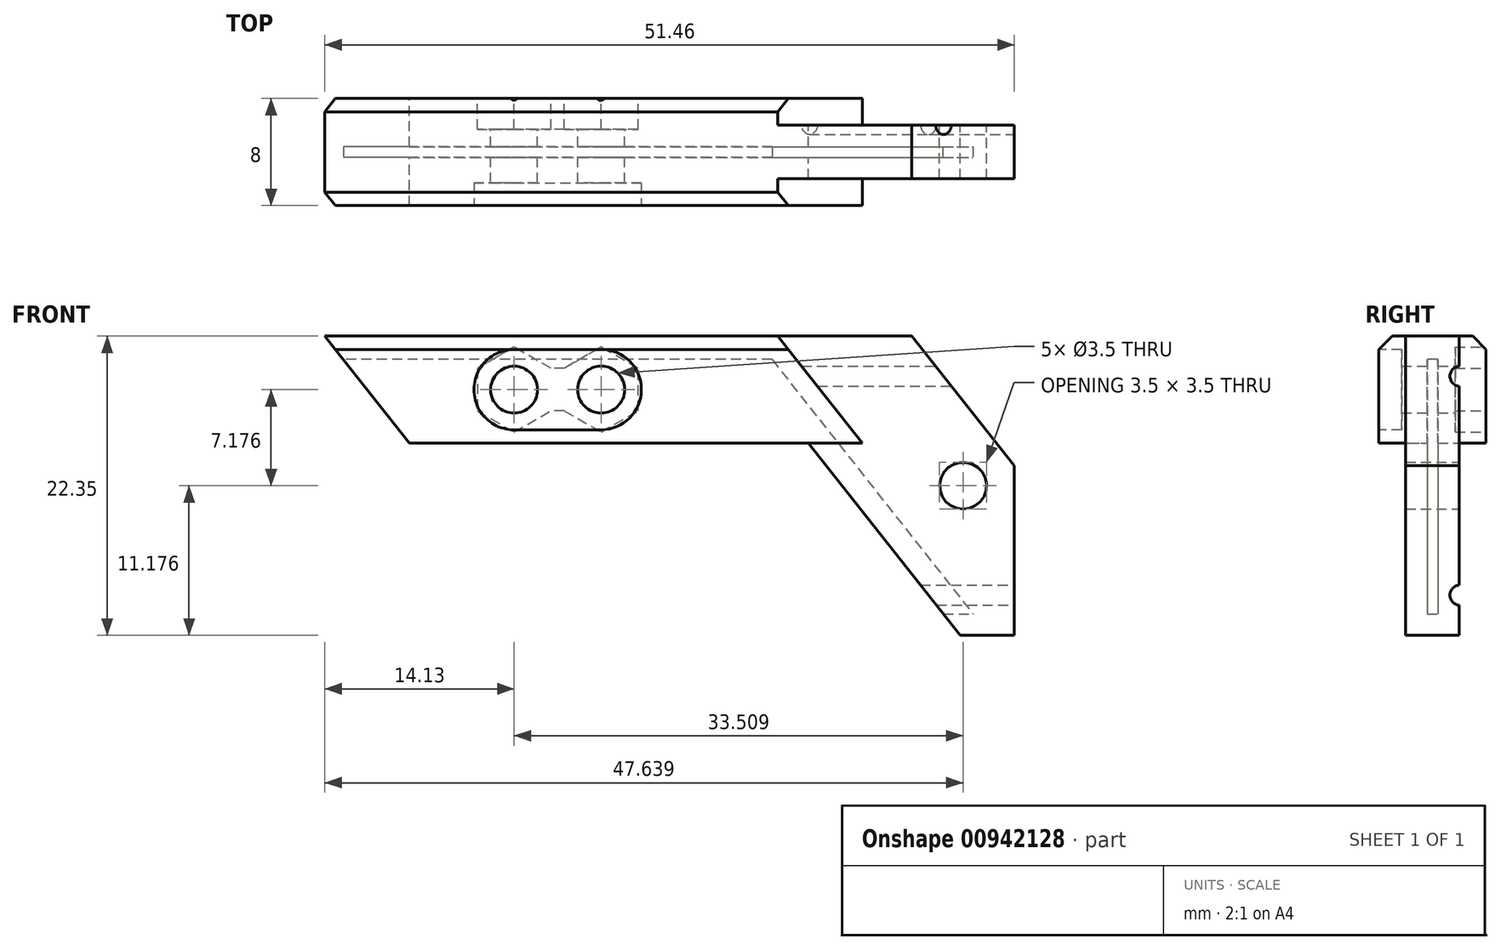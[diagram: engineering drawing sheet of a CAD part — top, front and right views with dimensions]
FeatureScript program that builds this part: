
annotation { "Feature Type Name" : "Feature", "Feature Type Description" : "" }
export const myFeature = defineFeature(function(context is Context, id is Id, definition is map)
    precondition{}
    {
        {
            var Q0;
            Q0=qCreatedBy(makeId("Front.planeOp"),FACE);
            var sketch = newSketch(context, id + "F0", { "sketchPlane" : qUnion([Q0])});
            skLineSegment(sketch, "E0", {"start": v(-31, 0) * mm, "end": v(31, 0) * mm});
            skLineSegment(sketch, "E1", {"start": v(31, 0) * mm, "end": v(31, 19) * mm, "construction": true});
            skLineSegment(sketch, "E2", {"start": v(31, 19) * mm, "end": v(-31, 19) * mm});
            skLineSegment(sketch, "E3", {"start": v(-16, 19) * mm, "end": v(16, 19) * mm});
            skPoint(sketch, "E4", {"position": v(0, 19) * mm});
            skLineSegment(sketch, "E5", {"start": v(16, 19) * mm, "end": v(31, 0) * mm});
            skLineSegment(sketch, "E6", {"start": v(-16, 19) * mm, "end": v(-31, 0) * mm});
            skLineSegment(sketch, "E7", {"start": v(-3.25, 19) * mm, "end": v(3.25, 19) * mm, "construction": true});
            skLineSegment(sketch, "E8", {"start": v(-3.25, 19) * mm, "end": v(-3.25, 15) * mm, "construction": true});
            skLineSegment(sketch, "E9", {"start": v(3.25, 19) * mm, "end": v(3.25, 15) * mm, "construction": true});
            skCircle(sketch, "E10", {"center": v(-3.25, 16.75) * mm, "radius": 1.75 * mm});
            skCircle(sketch, "E11", {"center": v(3.25, 16.75) * mm, "radius": 1.75 * mm});
            skLineSegment(sketch, "E12", {"start": v(-5, 16.81) * mm, "end": v(-5, 19) * mm});
            skLineSegment(sketch, "E13", {"start": v(-1.5, 16.8) * mm, "end": v(-1.5, 19) * mm});
            skLineSegment(sketch, "E14", {"start": v(1.5, 16.8) * mm, "end": v(1.5, 19) * mm});
            skLineSegment(sketch, "E15", {"start": v(5, 16.85) * mm, "end": v(5, 19) * mm});
            skSolve(sketch);
        }
        {
            var Q0;
            Q0=qCreatedBy(makeId("Front.planeOp"),FACE);
            var sketch = newSketch(context, id + "F1", { "sketchPlane" : qUnion([Q0])});
            skLineSegment(sketch, "E16.0.0", {"start": v(5, 19) * mm, "end": v(5, 16.85) * mm, "construction": true});
            skArc(sketch, "E16.0.1", {"start": v(5, 16.85) * mm, "mid": v(3.28, 15) * mm, "end": v(1.5, 16.8) * mm, "construction": true});
            skLineSegment(sketch, "E16.0.2", {"start": v(1.5, 16.8) * mm, "end": v(1.5, 19) * mm, "construction": true});
            skLineSegment(sketch, "E16.0.3", {"start": v(1.5, 19) * mm, "end": v(-1.5, 19) * mm, "construction": true});
            skLineSegment(sketch, "E16.0.4", {"start": v(-1.5, 19) * mm, "end": v(-1.5, 16.8) * mm, "construction": true});
            skArc(sketch, "E16.0.5", {"start": v(-1.5, 16.8) * mm, "mid": v(-3.26, 15) * mm, "end": v(-5, 16.81) * mm, "construction": true});
            skLineSegment(sketch, "E16.0.6", {"start": v(-5, 16.81) * mm, "end": v(-5, 19) * mm, "construction": true});
            skLineSegment(sketch, "E16.0.7", {"start": v(-5, 19) * mm, "end": v(-16, 19) * mm, "construction": true});
            skLineSegment(sketch, "E16.0.8", {"start": v(-16, 19) * mm, "end": v(-31, 0) * mm, "construction": true});
            skLineSegment(sketch, "E16.0.9", {"start": v(-31, 0) * mm, "end": v(31, 0) * mm, "construction": true});
            skLineSegment(sketch, "E16.0.10", {"start": v(31, 0) * mm, "end": v(16, 19) * mm, "construction": true});
            skLineSegment(sketch, "E16.0.11", {"start": v(16, 19) * mm, "end": v(5, 19) * mm, "construction": true});
            skLineSegment(sketch, "E17", {"start": v(-31, 0) * mm, "end": v(31, 0) * mm});
            skLineSegment(sketch, "E18", {"start": v(16, 19) * mm, "end": v(-16, 19) * mm});
            skLineSegment(sketch, "E19", {"start": v(-16, 19) * mm, "end": v(-31, 0) * mm});
            skLineSegment(sketch, "E20", {"start": v(16, 19) * mm, "end": v(31, 0) * mm});
            skSolve(sketch);
        }
        {
            var Q0;
            Q0=qCreatedBy(makeId("Front.planeOp"),FACE);
            var sketch = newSketch(context, id + "F2", { "sketchPlane" : qUnion([Q0])});
            skLineSegment(sketch, "E21.0.0", {"start": v(5, 19) * mm, "end": v(5, 16.85) * mm, "construction": true});
            skArc(sketch, "E21.0.1", {"start": v(5, 16.85) * mm, "mid": v(3.28, 15) * mm, "end": v(1.5, 16.8) * mm, "construction": true});
            skLineSegment(sketch, "E21.0.2", {"start": v(1.5, 16.8) * mm, "end": v(1.5, 19) * mm, "construction": true});
            skLineSegment(sketch, "E21.0.3", {"start": v(1.5, 19) * mm, "end": v(-1.5, 19) * mm, "construction": true});
            skLineSegment(sketch, "E21.0.4", {"start": v(-1.5, 19) * mm, "end": v(-1.5, 16.8) * mm, "construction": true});
            skArc(sketch, "E21.0.5", {"start": v(-1.5, 16.8) * mm, "mid": v(-3.26, 15) * mm, "end": v(-5, 16.81) * mm, "construction": true});
            skLineSegment(sketch, "E21.0.6", {"start": v(-5, 16.81) * mm, "end": v(-5, 19) * mm, "construction": true});
            skLineSegment(sketch, "E21.0.7", {"start": v(-5, 19) * mm, "end": v(-16, 19) * mm, "construction": true});
            skLineSegment(sketch, "E21.0.8", {"start": v(-16, 19) * mm, "end": v(-31, 0) * mm, "construction": true});
            skLineSegment(sketch, "E21.0.9", {"start": v(-31, 0) * mm, "end": v(31, 0) * mm, "construction": true});
            skLineSegment(sketch, "E21.0.10", {"start": v(31, 0) * mm, "end": v(16, 19) * mm, "construction": true});
            skLineSegment(sketch, "E21.0.11", {"start": v(16, 19) * mm, "end": v(5, 19) * mm, "construction": true});
            skLineSegment(sketch, "E22.0", {"start": v(-3.25, 19) * mm, "end": v(-3.25, 15) * mm, "construction": true});
            skLineSegment(sketch, "E22.1", {"start": v(31, 0) * mm, "end": v(31, 19) * mm, "construction": true});
            skLineSegment(sketch, "E22.2", {"start": v(3.25, 19) * mm, "end": v(3.25, 15) * mm, "construction": true});
            skLineSegment(sketch, "E22.3", {"start": v(31, 19) * mm, "end": v(-31, 19) * mm, "construction": true});
            skLineSegment(sketch, "E22.4", {"start": v(-16, 19) * mm, "end": v(16, 19) * mm, "construction": true});
            skCircle(sketch, "E22.5", {"center": v(-3.25, 16.75) * mm, "radius": 1.75 * mm, "construction": true});
            skCircle(sketch, "E22.6", {"center": v(3.25, 16.75) * mm, "radius": 1.75 * mm, "construction": true});
            skLineSegment(sketch, "E22.7", {"start": v(-3.25, 19) * mm, "end": v(3.25, 19) * mm, "construction": true});
            skLineSegment(sketch, "E22.10", {"start": v(-1.5, 16.8) * mm, "end": v(-1.5, 19) * mm, "construction": true});
            skLineSegment(sketch, "E22.11", {"start": v(16, 19) * mm, "end": v(31, 0) * mm, "construction": true});
            skLineSegment(sketch, "E22.14", {"start": v(5, 16.85) * mm, "end": v(5, 19) * mm, "construction": true});
            skCircle(sketch, "E23", {"center": v(-3.25, 16.75) * mm, "radius": 1.75 * mm});
            skCircle(sketch, "E24", {"center": v(3.25, 16.75) * mm, "radius": 1.75 * mm});
            skLineSegment(sketch, "E25", {"start": v(-16, 19) * mm, "end": v(-11.07, 12.75) * mm});
            skLineSegment(sketch, "E26", {"start": v(-11.07, 12.75) * mm, "end": v(20.93, 12.75) * mm});
            skCircle(sketch, "E27", {"center": v(-3.25, 16.75) * mm, "radius": 3 * mm});
            skCircle(sketch, "E28", {"center": v(3.25, 16.75) * mm, "radius": 3 * mm});
            skLineSegment(sketch, "E29", {"start": v(-16, 19) * mm, "end": v(-17.38, 20.75) * mm});
            skLineSegment(sketch, "E30", {"start": v(-17.38, 20.75) * mm, "end": v(14.62, 20.75) * mm});
            skLineSegment(sketch, "E31", {"start": v(16, 19) * mm, "end": v(14.62, 20.75) * mm});
            skLineSegment(sketch, "E32", {"start": v(18.72, 12.75) * mm, "end": v(30.05, -1.6) * mm});
            skLineSegment(sketch, "E33", {"start": v(30.05, -1.6) * mm, "end": v(34.08, -1.6) * mm});
            skLineSegment(sketch, "E34", {"start": v(34.08, -1.6) * mm, "end": v(16.44, 20.75) * mm});
            skLineSegment(sketch, "E35", {"start": v(16.44, 20.75) * mm, "end": v(14.62, 20.75) * mm});
            skLineSegment(sketch, "E36", {"start": v(16.44, 20.75) * mm, "end": v(26.44, 20.75) * mm});
            skLineSegment(sketch, "E37", {"start": v(26.44, 20.75) * mm, "end": v(44.08, -1.6) * mm});
            skLineSegment(sketch, "E38", {"start": v(22.75, 12.75) * mm, "end": v(32.75, 12.75) * mm});
            skLineSegment(sketch, "E39", {"start": v(32.75, 12.75) * mm, "end": v(26.44, 20.75) * mm});
            skLineSegment(sketch, "E40", {"start": v(16.44, 20.75) * mm, "end": v(22.75, 12.75) * mm});
            skLineSegment(sketch, "E41", {"start": v(37.84, -1.6) * mm, "end": v(37.84, 20.75) * mm, "construction": true});
            skLineSegment(sketch, "E42", {"start": v(37.84, 9.58) * mm, "end": v(14.7, 9.58) * mm, "construction": true});
            skLineSegment(sketch, "E43", {"start": v(25.26, 9.58) * mm, "end": v(35.26, 9.58) * mm, "construction": true});
            skCircle(sketch, "E44", {"center": v(30.26, 9.58) * mm, "radius": 1.75 * mm});
            skLineSegment(sketch, "E45", {"start": v(18.72, 12.75) * mm, "end": v(22.75, 12.75) * mm});
            skLineSegment(sketch, "E46", {"start": v(22.75, 12.75) * mm, "end": v(16.44, 20.75) * mm});
            skLineSegment(sketch, "E47", {"start": v(34.08, -1.6) * mm, "end": v(34.08, 11.07) * mm});
            skSolve(sketch);
        }
        {
            var Q0;
            Q0=qCreatedBy(makeId("Front.planeOp"),FACE);
            var sketch = newSketch(context, id + "F3", { "sketchPlane" : qUnion([Q0])});
            skLineSegment(sketch, "E48.0.0", {"start": v(14.62, 20.75) * mm, "end": v(14.62, 20.75) * mm});
            skLineSegment(sketch, "E48.0.1", {"start": v(14.62, 20.75) * mm, "end": v(-17.38, 20.75) * mm, "construction": true});
            skLineSegment(sketch, "E48.0.2", {"start": v(-17.38, 20.75) * mm, "end": v(-16, 19) * mm, "construction": true});
            skLineSegment(sketch, "E48.0.3", {"start": v(-16, 19) * mm, "end": v(-11.07, 12.75) * mm, "construction": true});
            skLineSegment(sketch, "E48.0.4", {"start": v(-11.07, 12.75) * mm, "end": v(18.72, 12.75) * mm, "construction": true});
            skLineSegment(sketch, "E48.0.5", {"start": v(18.72, 12.75) * mm, "end": v(30.05, -1.6) * mm, "construction": true});
            skLineSegment(sketch, "E48.0.6", {"start": v(30.05, -1.6) * mm, "end": v(34.08, -1.6) * mm, "construction": true});
            skLineSegment(sketch, "E48.0.7", {"start": v(34.08, -1.6) * mm, "end": v(16.44, 20.75) * mm, "construction": true});
            skLineSegment(sketch, "E49", {"start": v(30.05, -1.6) * mm, "end": v(18.72, 12.75) * mm});
            skLineSegment(sketch, "E50", {"start": v(-11.07, 12.75) * mm, "end": v(-17.38, 20.75) * mm});
            skLineSegment(sketch, "E51", {"start": v(-35.67, -1.6) * mm, "end": v(30.05, -1.6) * mm});
            skLineSegment(sketch, "E52", {"start": v(-11.07, 12.75) * mm, "end": v(18.72, 12.75) * mm});
            skLineSegment(sketch, "E53", {"start": v(-17.38, 20.75) * mm, "end": v(-35.67, -1.6) * mm});
            skLineSegment(sketch, "E54", {"start": v(18.72, 12.75) * mm, "end": v(32.74, 12.75) * mm});
            skLineSegment(sketch, "E55", {"start": v(32.74, 12.75) * mm, "end": v(44.07, -1.6) * mm});
            skLineSegment(sketch, "E56", {"start": v(44.07, -1.6) * mm, "end": v(30.05, -1.6) * mm});
            skLineSegment(sketch, "E57", {"start": v(14.62, 20.75) * mm, "end": v(14.62, -1.6) * mm, "construction": true});
            skLineSegment(sketch, "E58", {"start": v(14.62, 9.58) * mm, "end": v(40, 9.58) * mm, "construction": true});
            skLineSegment(sketch, "E59", {"start": v(25.26, 9.58) * mm, "end": v(35.25, 9.58) * mm, "construction": true});
            skCircle(sketch, "E60", {"center": v(30.25, 9.58) * mm, "radius": 1.75 * mm});
            skCircle(sketch, "E61", {"center": v(30.25, 9.58) * mm, "radius": 3 * mm});
            skSolve(sketch);
        }
        {
            var Q0;
            {var subQ3=sQuery(id+"F2.wireOp",EDGE,"E25");Q0=makeQuery(id+"F2.imprint","IMPRINT",FACE,{"disambiguationData":[TD([[makeQuery(id+"F2.imprint","IMPRINT",EDGE,{"derivedFrom":subQ3}),1.0]])]});}
            var Q1;
            Q1=makeQuery(id+"F2.imprint","IMPRINT",FACE,{"disambiguationData":[TD([[makeQuery(id+"F2.imprint","IMPRINT",EDGE,{"derivedFrom":sQuery(id+"F2.wireOp",EDGE,"E24")}),-1.0]])]});
            var Q2;
            Q2=makeQuery(id+"F2.imprint","IMPRINT",FACE,{"disambiguationData":[TD([[makeQuery(id+"F2.imprint","IMPRINT",EDGE,{"derivedFrom":sQuery(id+"F2.wireOp",EDGE,"E23")}),-1.0]])]});
            extrude(context, id + "F4", {"entities" : qUnion([Q0, Q1, Q2]), "depth" : 4 * mm, "offsetDistance" : 25 * mm, "hasSecondDirection" : true, "secondDirectionOppositeDirection" : true, "secondDirectionDepth" : 4 * mm});
        }
        {
            var Q0;
            {var subQ0=sQuery(id+"F2.wireOp",EDGE,"E36");Q0=makeQuery(id+"F2.imprint","IMPRINT",FACE,{"disambiguationData":[TD([[makeQuery(id+"F2.imprint","IMPRINT",EDGE,{"derivedFrom":subQ0}),-1.0]])]});}
            var Q1;
            {var subQ0=sQuery(id+"F2.wireOp",EDGE,"E38");Q1=makeQuery(id+"F2.imprint","IMPRINT",FACE,{"disambiguationData":[TD([[makeQuery(id+"F2.imprint","IMPRINT",EDGE,{"derivedFrom":subQ0}),-1.0]])]});}
            var Q2;
            Q2=makeQuery(id+"F3.imprint","IMPRINT",FACE,{"disambiguationData":[TD([[makeQuery(id+"F3.imprint","IMPRINT",EDGE,{"derivedFrom":sQuery(id+"F3.wireOp",EDGE,"E60")}),-1.0]])]});
            var Q3;
            {var subQ3=sQuery(id+"F2.wireOp",EDGE,"E32");Q3=makeQuery(id+"F2.imprint","IMPRINT",FACE,{"disambiguationData":[TD([[makeQuery(id+"F2.imprint","IMPRINT",EDGE,{"derivedFrom":subQ3}),1.0]])]});}
            extrude(context, id + "F5", {"entities" : qUnion([Q0, Q1, Q2, Q3]), "operationType" : NewBodyOperationType.ADD, "depth" : 2 * mm, "offsetDistance" : 25 * mm, "hasSecondDirection" : true, "secondDirectionOppositeDirection" : true, "secondDirectionDepth" : 2 * mm});
        }
        {
            var Q0;
            Q0 = qSketchRegion(id + "F1", true);
            extrude(context, id + "F6", {"entities" : qUnion([Q0]), "operationType" : NewBodyOperationType.REMOVE, "oppositeDirection" : true, "depth" : 0.4 * mm, "offsetDistance" : 25 * mm, "hasSecondDirection" : true, "secondDirectionOppositeDirection" : false, "secondDirectionDepth" : 0.4 * mm});
        }
        {
            var Q0;
            Q0=makeQuery(id+"F4.opExtrude","CAP_FACE",FACE,{"disambiguationData":[OSD([sQuery(id+"F2.wireOp",EDGE,"E23"),sQuery(id+"F2.wireOp",EDGE,"E24"),sQuery(id+"F2.wireOp",EDGE,"E25"),sQuery(id+"F2.wireOp",EDGE,"E26"),sQuery(id+"F2.wireOp",EDGE,"E29"),sQuery(id+"F2.wireOp",EDGE,"E30"),sQuery(id+"F2.wireOp",EDGE,"E34"),sQuery(id+"F2.wireOp",EDGE,"E35"),sQuery(id+"F2.wireOp",EDGE,"E45")])],"isStart":false});
            var sketch = newSketch(context, id + "F7", { "sketchPlane" : qUnion([Q0])});
            skCircle(sketch, "E62.0", {"center": v(3.25, 16.75) * mm, "radius": 3 * mm});
            skCircle(sketch, "E63.0", {"center": v(-3.25, 16.75) * mm, "radius": 3 * mm});
            skLineSegment(sketch, "E64", {"start": v(-3.25, 19.75) * mm, "end": v(3.25, 19.75) * mm});
            skLineSegment(sketch, "E65", {"start": v(-3.25, 13.75) * mm, "end": v(3.25, 13.75) * mm});
            skSolve(sketch);
        }
        {
            var Q0;
            Q0=makeQuery(id+"F7.imprint","IMPRINT",FACE,{"disambiguationData":[TD([[makeQuery(id+"F7.imprint","IMPRINT",EDGE,{"derivedFrom":sQuery(id+"F7.wireOp",EDGE,"E62.0")}),1.0]])]});
            var Q1;
            Q1=makeQuery(id+"F7.imprint","IMPRINT",FACE,{"disambiguationData":[TD([[makeQuery(id+"F7.imprint","IMPRINT",EDGE,{"derivedFrom":sQuery(id+"F7.wireOp",EDGE,"E63.0")}),1.0]])]});
            var Q2;
            {var subQ0=sQuery(id+"F7.wireOp",EDGE,"E64");Q2=makeQuery(id+"F7.imprint","IMPRINT",FACE,{"disambiguationData":[TD([[makeQuery(id+"F7.imprint","IMPRINT",EDGE,{"derivedFrom":subQ0}),-1.0]])]});}
            extrude(context, id + "F8", {"entities" : qUnion([Q0, Q1, Q2]), "operationType" : NewBodyOperationType.REMOVE, "oppositeDirection" : true, "depth" : 1.7 * mm, "offsetDistance" : 25 * mm});
        }
        {
            var Q0;
            Q0=makeQuery(id+"F4.opExtrude","CAP_FACE",FACE,{"disambiguationData":[OSD([sQuery(id+"F2.wireOp",EDGE,"E23"),sQuery(id+"F2.wireOp",EDGE,"E24"),sQuery(id+"F2.wireOp",EDGE,"E25"),sQuery(id+"F2.wireOp",EDGE,"E26"),sQuery(id+"F2.wireOp",EDGE,"E29"),sQuery(id+"F2.wireOp",EDGE,"E30"),sQuery(id+"F2.wireOp",EDGE,"E34"),sQuery(id+"F2.wireOp",EDGE,"E35"),sQuery(id+"F2.wireOp",EDGE,"E45")])],"isStart":true});
            var sketch = newSketch(context, id + "F9", { "sketchPlane" : qUnion([Q0])});
            skPoint(sketch, "E66.0", {"position": v(-3.25, 16.75) * mm});
            skPoint(sketch, "E67.0", {"position": v(3.25, 16.75) * mm});
            skCircle(sketch, "E68.cCircle", {"center": v(-3.25, 16.75) * mm, "radius": 2.75 * mm, "construction": true});
            skLineSegment(sketch, "E68.0", {"start": v(-0.5, 18.34) * mm, "end": v(-0.5, 15.16) * mm});
            skLineSegment(sketch, "E68.1", {"start": v(-0.5, 15.16) * mm, "end": v(-3.25, 13.58) * mm});
            skLineSegment(sketch, "E68.2", {"start": v(-3.25, 13.58) * mm, "end": v(-6, 15.17) * mm});
            skLineSegment(sketch, "E68.3", {"start": v(-6, 15.17) * mm, "end": v(-6, 18.34) * mm});
            skLineSegment(sketch, "E68.4", {"start": v(-6, 18.34) * mm, "end": v(-3.25, 19.93) * mm});
            skLineSegment(sketch, "E68.5", {"start": v(-3.25, 19.93) * mm, "end": v(-0.5, 18.34) * mm});
            skPoint(sketch, "E68.0.midPoint", {"position": v(-0.5, 16.75) * mm});
            skCircle(sketch, "E69.cCircle", {"center": v(3.25, 16.75) * mm, "radius": 2.75 * mm, "construction": true});
            skLineSegment(sketch, "E69.0", {"start": v(0.5, 15.16) * mm, "end": v(0.5, 18.34) * mm});
            skLineSegment(sketch, "E69.1", {"start": v(0.5, 18.34) * mm, "end": v(3.25, 19.92) * mm});
            skLineSegment(sketch, "E69.2", {"start": v(3.25, 19.92) * mm, "end": v(6, 18.33) * mm});
            skLineSegment(sketch, "E69.3", {"start": v(6, 18.33) * mm, "end": v(6, 15.16) * mm});
            skLineSegment(sketch, "E69.4", {"start": v(6, 15.16) * mm, "end": v(3.25, 13.57) * mm});
            skLineSegment(sketch, "E69.5", {"start": v(3.25, 13.57) * mm, "end": v(0.5, 15.16) * mm});
            skPoint(sketch, "E69.0.midPoint", {"position": v(0.5, 16.75) * mm});
            skLineSegment(sketch, "E70", {"start": v(-0.5, 18.34) * mm, "end": v(0.5, 18.34) * mm});
            skLineSegment(sketch, "E71", {"start": v(-0.5, 15.16) * mm, "end": v(0.5, 15.16) * mm});
            skSolve(sketch);
        }
        {
            var Q0;
            Q0=makeQuery(id+"F9.imprint","IMPRINT",FACE,{"disambiguationData":[TD([[makeQuery(id+"F9.imprint","IMPRINT",EDGE,{"derivedFrom":sQuery(id+"F9.wireOp",EDGE,"E68.0")}),-1.0]])]});
            var Q1;
            Q1=makeQuery(id+"F9.imprint","IMPRINT",FACE,{"disambiguationData":[TD([[makeQuery(id+"F9.imprint","IMPRINT",EDGE,{"derivedFrom":sQuery(id+"F9.wireOp",EDGE,"E68.0")}),1.0]])]});
            var Q2;
            Q2=makeQuery(id+"F9.imprint","IMPRINT",FACE,{"disambiguationData":[TD([[makeQuery(id+"F9.imprint","IMPRINT",EDGE,{"derivedFrom":sQuery(id+"F9.wireOp",EDGE,"E69.0")}),-1.0]])]});
            extrude(context, id + "F10", {"entities" : qUnion([Q0, Q1, Q2]), "operationType" : NewBodyOperationType.REMOVE, "oppositeDirection" : true, "depth" : 2.3 * mm, "offsetDistance" : 25 * mm});
        }
        {
            var Q0;
            Q0=makeQuery(id+"F4.opExtrude","CAP_EDGE",EDGE,{"disambiguationData":[OSD([sQuery(id+"F2.wireOp",EDGE,"E30"),sQuery(id+"F2.wireOp",EDGE,"E35")])],"isStart":false});
            var Q1;
            Q1=makeQuery(id+"F4.opExtrude","CAP_EDGE",EDGE,{"disambiguationData":[OSD([sQuery(id+"F2.wireOp",EDGE,"E30"),sQuery(id+"F2.wireOp",EDGE,"E35")])],"isStart":true});
            chamfer(context, id + "F11", {"entities" : qUnion([Q0, Q1]), "width" : 1 * mm, "tangentPropagation" : true});
        }
        {
            var Q0;
            Q0=makeQuery(id+"F5.opExtrude","SWEPT_FACE",FACE,{"disambiguationData":[OSD([sQuery(id+"F2.wireOp",EDGE,"E47")])]});
            var sketch = newSketch(context, id + "F12", { "sketchPlane" : qUnion([Q0])});
            skLineSegment(sketch, "E72", {"start": v(2, 2.15) * mm, "end": v(2, 0.65) * mm, "construction": true});
            skLineSegment(sketch, "E73", {"start": v(2, 1.4) * mm, "end": v(1.3, 1.4) * mm, "construction": true});
            skArc(sketch, "E74", {"start": v(2, 2.15) * mm, "mid": v(1.3, 1.4) * mm, "end": v(2, 0.65) * mm});
            skLineSegment(sketch, "E75", {"start": v(2, 2.15) * mm, "end": v(2, 0.65) * mm});
            skSolve(sketch);
        }
        {
            var Q0;
            Q0 = qSketchRegion(id + "F12", true);
            extrude(context, id + "F13", {"entities" : qUnion([Q0]), "operationType" : NewBodyOperationType.REMOVE, "endBound" : BoundingType.THROUGH_ALL, "oppositeDirection" : true, "depth" : 25 * mm, "offsetDistance" : 25 * mm});
        }
        {
            var Q0;
            Q0=makeQuery(id+"F5.opExtrude","SWEPT_FACE",FACE,{"disambiguationData":[OSD([sQuery(id+"F2.wireOp",EDGE,"E47")])]});
            var sketch = newSketch(context, id + "F14", { "sketchPlane" : qUnion([Q0])});
            skLineSegment(sketch, "E76.0.0", {"start": v(2, 11.07) * mm, "end": v(2, 20.75) * mm, "construction": true});
            skLineSegment(sketch, "E77", {"start": v(2, 18.5) * mm, "end": v(2, 17) * mm});
            skLineSegment(sketch, "E78", {"start": v(2, 17.75) * mm, "end": v(1.3, 17.75) * mm, "construction": true});
            skArc(sketch, "E79", {"start": v(2, 18.5) * mm, "mid": v(1.3, 17.75) * mm, "end": v(2, 17) * mm});
            skSolve(sketch);
        }
        {
            var Q0;
            Q0=makeQuery(id+"F14.imprint","IMPRINT",FACE,{"disambiguationData":[TD([[makeQuery(id+"F14.imprint","IMPRINT",EDGE,{"derivedFrom":sQuery(id+"F14.wireOp",EDGE,"E77")}),-1.0]])]});
            var Q1;
            {var subQ0=sQuery(id+"F2.wireOp",EDGE,"E45");var subQ1=sQuery(id+"F2.wireOp",EDGE,"E26");var subQ3=sQuery(id+"F2.wireOp",EDGE,"E34");var subQ4=sQuery(id+"F2.wireOp",EDGE,"E35");var subQ5=sQuery(id+"F2.wireOp",EDGE,"E30");Q1=makeQuery(id+"F5.boolean.opBoolean","SPLIT",FACE,{"disambiguationData":[TD([makeQuery(id+"F4.opExtrude","CAP_FACE",FACE,{"disambiguationData":[OSD([sQuery(id+"F2.wireOp",EDGE,"E23"),sQuery(id+"F2.wireOp",EDGE,"E24"),sQuery(id+"F2.wireOp",EDGE,"E25"),subQ1,sQuery(id+"F2.wireOp",EDGE,"E29"),subQ5,subQ3,subQ4,subQ0])],"isStart":true})])],"derivedFrom":makeQuery(id+"F4.opExtrude","SWEPT_FACE",FACE,{"disambiguationData":[OSD([subQ3])]})});}
            extrude(context, id + "F15", {"entities" : qUnion([Q0]), "operationType" : NewBodyOperationType.REMOVE, "endBound" : BoundingType.UP_TO_SURFACE, "oppositeDirection" : true, "depth" : 25 * mm, "endBoundEntityFace" : qUnion([Q1]), "offsetDistance" : 25 * mm});
        }
    });
